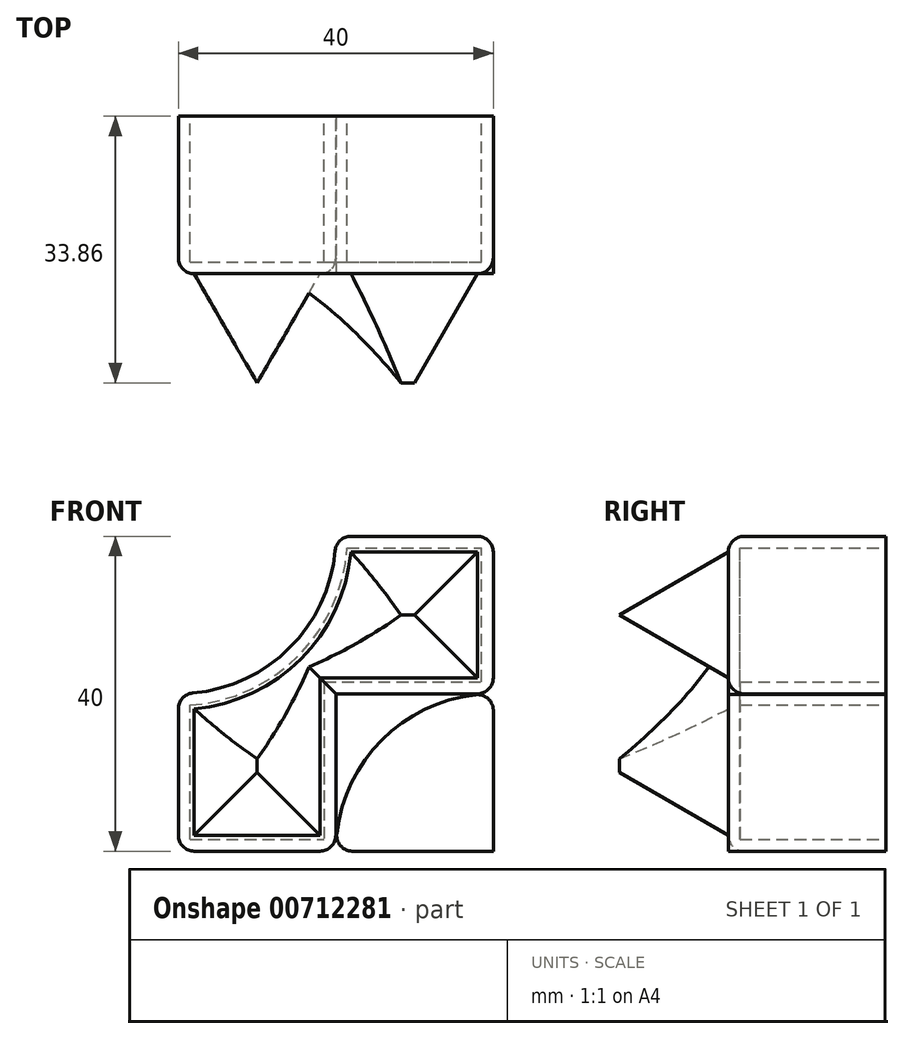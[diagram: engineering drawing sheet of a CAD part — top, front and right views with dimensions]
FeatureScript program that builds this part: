
annotation { "Feature Type Name" : "Feature", "Feature Type Description" : "" }
export const myFeature = defineFeature(function(context is Context, id is Id, definition is map)
    precondition{}
    {
        {
            var Q0;
            Q0=qCreatedBy(makeId("Front.planeOp"),FACE);
            var sketch = newSketch(context, id + "F0", { "sketchPlane" : qUnion([Q0])});
            skLineSegment(sketch, "E0.bottom", {"start": v(0, 0) * mm, "end": v(40, 0) * mm});
            skLineSegment(sketch, "E0.top", {"start": v(0, 40) * mm, "end": v(40, 40) * mm});
            skLineSegment(sketch, "E0.left", {"start": v(0, 0) * mm, "end": v(0, 40) * mm});
            skLineSegment(sketch, "E0.right", {"start": v(40, 0) * mm, "end": v(40, 40) * mm});
            skArc(sketch, "E1", {"start": v(0, 20) * mm, "mid": v(14.14, 25.86) * mm, "end": v(20, 40) * mm});
            skArc(sketch, "E2", {"start": v(20, 0) * mm, "mid": v(25.86, 14.14) * mm, "end": v(40, 20) * mm});
            skLineSegment(sketch, "E3", {"start": v(20, 40) * mm, "end": v(20, 0) * mm});
            skLineSegment(sketch, "E4", {"start": v(0, 20) * mm, "end": v(40, 20) * mm});
            skSolve(sketch);
        }
        {
            var Q0;
            {var subQ0=sQuery(id+"F0.wireOp",EDGE,"E0.right");var subQ1=sQuery(id+"F0.wireOp",EDGE,"E0.top");var subQ2=makeQuery(id+"F0.imprint","INTERSECT",VERTEX,{"derivedFrom":[subQ1,subQ0]});Q0=makeQuery(id+"F0.imprint","IMPRINT",FACE,{"disambiguationData":[TD([[makeQuery(id+"F0.imprint","IMPRINT",EDGE,{"disambiguationData":[TD([[subQ2,1.0]])],"derivedFrom":subQ1}),-1.0]])]});}
            var Q1;
            {var subQ0=sQuery(id+"F0.wireOp",EDGE,"E2");Q1=makeQuery(id+"F0.imprint","IMPRINT",FACE,{"disambiguationData":[TD([[makeQuery(id+"F0.imprint","IMPRINT",EDGE,{"derivedFrom":subQ0}),1.0]])]});}
            var Q2;
            {var subQ0=sQuery(id+"F0.wireOp",EDGE,"E0.left");var subQ1=sQuery(id+"F0.wireOp",EDGE,"E0.bottom");var subQ2=makeQuery(id+"F0.imprint","INTERSECT",VERTEX,{"derivedFrom":[subQ1,subQ0]});Q2=makeQuery(id+"F0.imprint","IMPRINT",FACE,{"disambiguationData":[TD([[makeQuery(id+"F0.imprint","IMPRINT",EDGE,{"disambiguationData":[TD([[subQ2,-1.0]])],"derivedFrom":subQ1}),1.0]])]});}
            var Q3;
            {var subQ0=sQuery(id+"F0.wireOp",EDGE,"E1");Q3=makeQuery(id+"F0.imprint","IMPRINT",FACE,{"disambiguationData":[TD([[makeQuery(id+"F0.imprint","IMPRINT",EDGE,{"derivedFrom":subQ0}),-1.0]])]});}
            extrude(context, id + "F1", {"entities" : qUnion([Q0, Q1, Q2, Q3]), "depth" : 20 * mm, "offsetDistance" : 25 * mm});
        }
        {
            var Q0;
            Q0=makeQuery(id+"F1.opExtrude","CAP_FACE",FACE,{"disambiguationData":[OSD([sQuery(id+"F0.wireOp",EDGE,"E0.bottom"),sQuery(id+"F0.wireOp",EDGE,"E0.top"),sQuery(id+"F0.wireOp",EDGE,"E0.left"),sQuery(id+"F0.wireOp",EDGE,"E0.right"),sQuery(id+"F0.wireOp",EDGE,"E1"),sQuery(id+"F0.wireOp",EDGE,"E2")])],"isStart":true});
            shell(context, id + "F2", {"entities" : qUnion([Q0]), "thickness" : 1.5 * mm});
        }
        {
            var Q0;
            Q0=makeQuery(id+"F1.opExtrude","CAP_FACE",FACE,{"disambiguationData":[OSD([sQuery(id+"F0.wireOp",EDGE,"E0.bottom"),sQuery(id+"F0.wireOp",EDGE,"E0.top"),sQuery(id+"F0.wireOp",EDGE,"E0.left"),sQuery(id+"F0.wireOp",EDGE,"E0.right"),sQuery(id+"F0.wireOp",EDGE,"E1"),sQuery(id+"F0.wireOp",EDGE,"E2")])],"isStart":false});
            var Q1;
            Q1=makeQuery(id+"F1.opExtrude","SWEPT_EDGE",EDGE,{"disambiguationData":[OSD([sQuery(id+"F0.wireOp",EDGE,"E0.bottom"),sQuery(id+"F0.wireOp",EDGE,"E2")])]});
            var Q2;
            Q2=makeQuery(id+"F1.opExtrude","SWEPT_EDGE",EDGE,{"disambiguationData":[OSD([sQuery(id+"F0.wireOp",EDGE,"E0.bottom"),sQuery(id+"F0.wireOp",EDGE,"E0.left")])]});
            var Q3;
            Q3=makeQuery(id+"F1.opExtrude","SWEPT_EDGE",EDGE,{"disambiguationData":[OSD([sQuery(id+"F0.wireOp",EDGE,"E0.right"),sQuery(id+"F0.wireOp",EDGE,"E2")])]});
            var Q4;
            Q4=makeQuery(id+"F1.opExtrude","SWEPT_EDGE",EDGE,{"disambiguationData":[OSD([sQuery(id+"F0.wireOp",EDGE,"E0.top"),sQuery(id+"F0.wireOp",EDGE,"E0.right")])]});
            var Q5;
            Q5=makeQuery(id+"F1.opExtrude","SWEPT_EDGE",EDGE,{"disambiguationData":[OSD([sQuery(id+"F0.wireOp",EDGE,"E0.top"),sQuery(id+"F0.wireOp",EDGE,"E1")])]});
            var Q6;
            Q6=makeQuery(id+"F1.opExtrude","SWEPT_EDGE",EDGE,{"disambiguationData":[OSD([sQuery(id+"F0.wireOp",EDGE,"E0.left"),sQuery(id+"F0.wireOp",EDGE,"E1")])]});
            fillet(context, id + "F3", {"entities" : qUnion([Q0, Q1, Q2, Q3, Q4, Q5, Q6]), "radius" : 2 * mm, "tangentPropagation" : true, "allowEdgeOverflow" : false});
        }
        {
            var Q0;
            Q0=makeQuery(id+"F1.opExtrude","CAP_FACE",FACE,{"disambiguationData":[OSD([sQuery(id+"F0.wireOp",EDGE,"E0.bottom"),sQuery(id+"F0.wireOp",EDGE,"E0.top"),sQuery(id+"F0.wireOp",EDGE,"E0.left"),sQuery(id+"F0.wireOp",EDGE,"E0.right"),sQuery(id+"F0.wireOp",EDGE,"E1"),sQuery(id+"F0.wireOp",EDGE,"E2")])],"isStart":false});
            extrude(context, id + "F4", {"entities" : qUnion([Q0]), "operationType" : NewBodyOperationType.ADD, "depth" : 50 * mm, "offsetDistance" : 25 * mm, "hasDraft" : true, "draftAngle" : 30 * degree, "draftPullDirection" : true});
        }
    });
